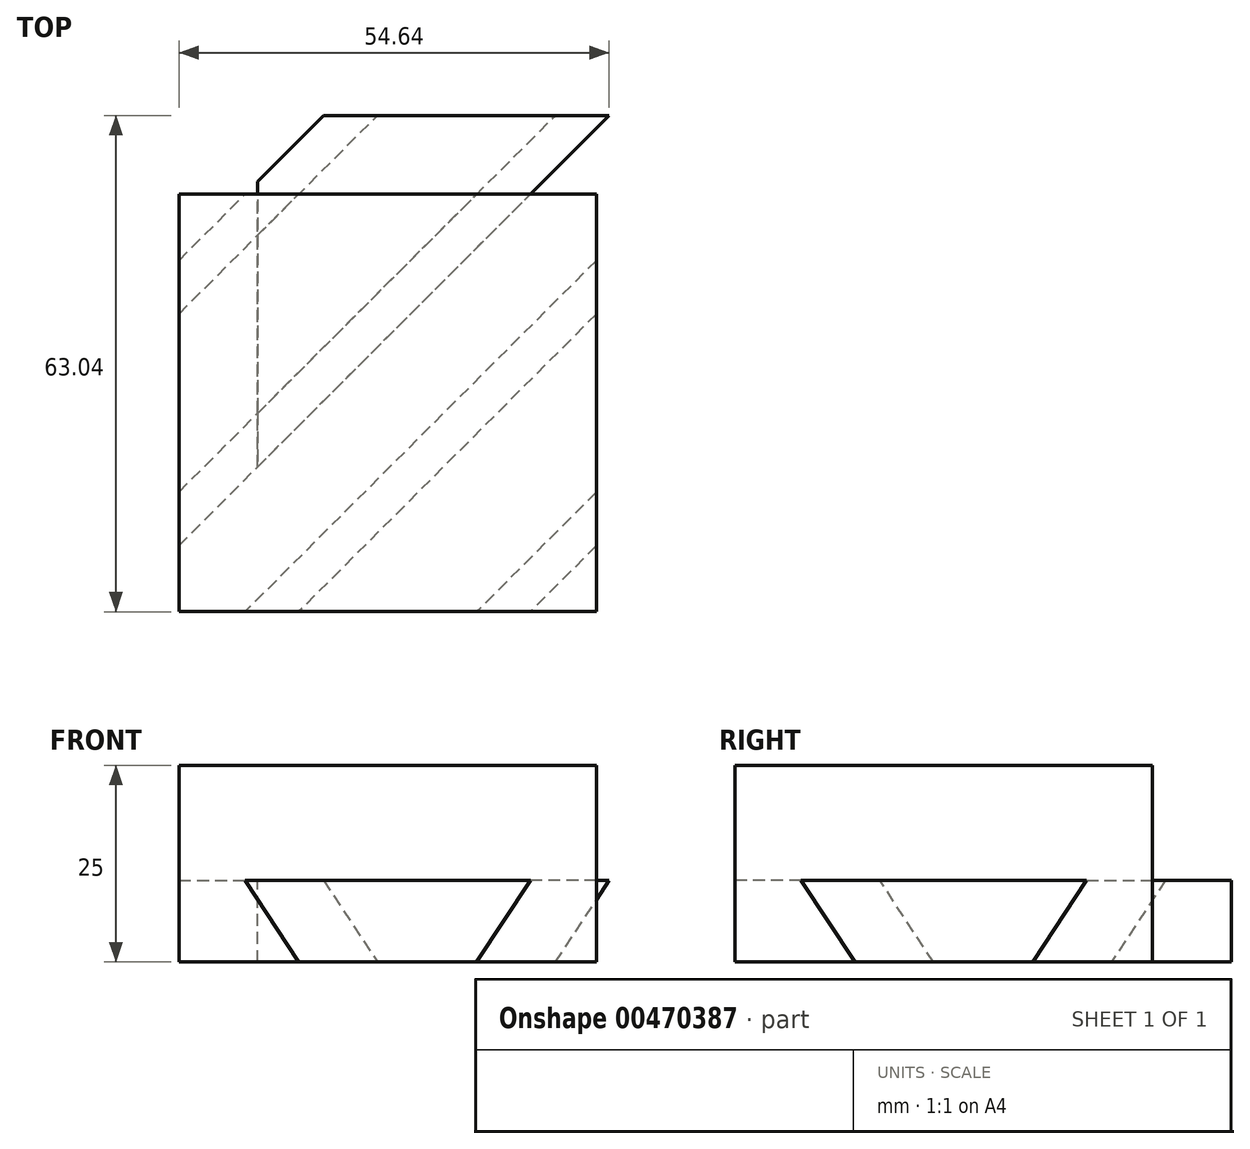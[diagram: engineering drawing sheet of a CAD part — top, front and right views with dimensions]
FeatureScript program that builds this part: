
annotation { "Feature Type Name" : "Feature", "Feature Type Description" : "" }
export const myFeature = defineFeature(function(context is Context, id is Id, definition is map)
    precondition{}
    {
        {
            var Q0;
            Q0=qCreatedBy(makeId("Top.planeOp"),FACE);
            var sketch = newSketch(context, id + "F0", { "sketchPlane" : qUnion([Q0])});
            skLineSegment(sketch, "E0.bottom", {"start": v(26.52, -26.52) * mm, "end": v(-26.52, -26.52) * mm});
            skLineSegment(sketch, "E0.top", {"start": v(26.52, 26.52) * mm, "end": v(-26.52, 26.52) * mm});
            skLineSegment(sketch, "E0.left", {"start": v(26.52, -26.52) * mm, "end": v(26.52, 26.52) * mm});
            skLineSegment(sketch, "E0.right", {"start": v(-26.52, -26.52) * mm, "end": v(-26.52, 26.52) * mm});
            skPoint(sketch, "E0.middle", {"position": v(0, 0) * mm});
            skSolve(sketch);
        }
        {
            var Q0;
            Q0=makeQuery(id+"F0.imprint","IMPRINT",FACE,{"disambiguationData":[TD([[makeQuery(id+"F0.imprint","IMPRINT",EDGE,{"derivedFrom":sQuery(id+"F0.wireOp",EDGE,"E0.bottom")}),-1.0]])]});
            extrude(context, id + "F1", {"entities" : qUnion([Q0]), "depth" : 25 * mm, "offsetDistance" : 25 * mm});
        }
        {
            var Q0;
            Q0=makeQuery(id+"F1.opExtrude","SWEPT_FACE",FACE,{"disambiguationData":[OSD([sQuery(id+"F0.wireOp",EDGE,"E0.bottom")])]});
            var sketch = newSketch(context, id + "F2", { "sketchPlane" : qUnion([Q0])});
            skLineSegment(sketch, "E1", {"start": v(-11.31, 25) * mm, "end": v(-18.12, 35.36) * mm});
            skLineSegment(sketch, "E2", {"start": v(-18.12, 35.36) * mm, "end": v(18.12, 35.36) * mm});
            skLineSegment(sketch, "E3", {"start": v(18.12, 35.36) * mm, "end": v(11.31, 25) * mm});
            skLineSegment(sketch, "E4", {"start": v(11.31, 25) * mm, "end": v(-11.31, 25) * mm});
            skPoint(sketch, "E5", {"position": v(0, 25) * mm});
            skLineSegment(sketch, "E6", {"start": v(0, 0) * mm, "end": v(0, 25) * mm, "construction": true});
            skSolve(sketch);
        }
        {
            var Q0;
            Q0=sQuery(id+"F2.wireOp",EDGE,"E6");
            cPlane(context, id + "F3", {"entities" : qUnion([Q0]), "cplaneType" : CPlaneType.LINE_ANGLE, "offset" : 25 * mm, "angle" : 45 * degree, "width" : 150 * mm, "height" : 150 * mm});
        }
        {
            var Q0;
            Q0=qCreatedBy(id+"F3.planeOp",FACE);
            var sketch = newSketch(context, id + "F4", { "sketchPlane" : qUnion([Q0])});
            skLineSegment(sketch, "E7.0.0", {"start": v(-5.94, 35.36) * mm, "end": v(-10.75, 25) * mm});
            skLineSegment(sketch, "E7.0.1", {"start": v(-10.75, 25) * mm, "end": v(-26.75, 25) * mm});
            skLineSegment(sketch, "E7.0.2", {"start": v(-26.75, 25) * mm, "end": v(-31.56, 35.36) * mm});
            skLineSegment(sketch, "E7.0.3", {"start": v(-31.56, 35.36) * mm, "end": v(-5.94, 35.36) * mm});
            skSolve(sketch);
        }
        {
            var Q0;
            Q0=makeQuery(id+"F1.opExtrude","CAP_FACE",FACE,{"disambiguationData":[OSD([sQuery(id+"F0.wireOp",EDGE,"E0.bottom"),sQuery(id+"F0.wireOp",EDGE,"E0.top"),sQuery(id+"F0.wireOp",EDGE,"E0.left"),sQuery(id+"F0.wireOp",EDGE,"E0.right")])],"isStart":false});
            extrude(context, id + "F5", {"entities" : qUnion([Q0]), "depth" : 41.2 * mm, "offsetDistance" : 25 * mm});
        }
        {
            var Q0;
            Q0=makeQuery(id+"F4.imprint","IMPRINT",FACE,{"disambiguationData":[TD([[makeQuery(id+"F4.imprint","IMPRINT",EDGE,{"derivedFrom":sQuery(id+"F4.wireOp",EDGE,"E7.0.0")}),-1.0]])]});
            extrude(context, id + "F6", {"entities" : qUnion([Q0]), "endBound" : BoundingType.SYMMETRIC, "depth" : 119 * mm, "offsetDistance" : 25 * mm});
        }
        {
            var Q0;
            Q0=makeQuery(id+"F1.opExtrude","CAP_FACE",FACE,{"disambiguationData":[OSD([sQuery(id+"F0.wireOp",EDGE,"E0.bottom"),sQuery(id+"F0.wireOp",EDGE,"E0.top"),sQuery(id+"F0.wireOp",EDGE,"E0.left"),sQuery(id+"F0.wireOp",EDGE,"E0.right")])],"isStart":false});
            extrude(context, id + "F7", {"entities" : qUnion([Q0]), "operationType" : NewBodyOperationType.INTERSECT, "depth" : 25 * mm, "offsetDistance" : 25 * mm});
        }
        {
            var Q0;
            Q0=qCreatedBy(makeId("Front.planeOp"),FACE);
            var sketch = newSketch(context, id + "F8", { "sketchPlane" : qUnion([Q0])});
            skLineSegment(sketch, "E8", {"start": v(0, 0) * mm, "end": v(0, 56.28) * mm, "construction": true});
            skSolve(sketch);
        }
        {
            var Q0;
            Q0=makeQuery(id+"F6.opExtrude","SWEPT_BODY",BODY,{"disambiguationData":[OSD([sQuery(id+"F4.wireOp",EDGE,"E7.0.0"),sQuery(id+"F4.wireOp",EDGE,"E7.0.1"),sQuery(id+"F4.wireOp",EDGE,"E7.0.2"),sQuery(id+"F4.wireOp",EDGE,"E7.0.3")])]});
            var Q1;
            Q1=sQuery(id+"F8.wireOp",EDGE,"E8");
            transform(context, id + "F9", {"entities" : qUnion([Q0]), "transformType" : TransformType.ROTATION, "transformAxis" : qUnion([Q1]), "angle" : 180 * degree, "makeCopy" : true});
        }
        {
            var Q0;
            Q0=makeQuery(id+"F9.opPattern","COPY",BODY,{"derivedFrom":makeQuery(id+"F6.opExtrude","SWEPT_BODY",BODY,{"disambiguationData":[OSD([sQuery(id+"F4.wireOp",EDGE,"E7.0.0"),sQuery(id+"F4.wireOp",EDGE,"E7.0.1"),sQuery(id+"F4.wireOp",EDGE,"E7.0.2"),sQuery(id+"F4.wireOp",EDGE,"E7.0.3")])]}),"instanceName":"1"});
            transform(context, id + "F10", {"entities" : qUnion([Q0]), "transformType" : TransformType.COPY});
        }
        {
            var Q0;
            Q0=makeQuery(id+"F10.opPattern","COPY",BODY,{"derivedFrom":makeQuery(id+"F9.opPattern","COPY",BODY,{"derivedFrom":makeQuery(id+"F6.opExtrude","SWEPT_BODY",BODY,{"disambiguationData":[OSD([sQuery(id+"F4.wireOp",EDGE,"E7.0.0"),sQuery(id+"F4.wireOp",EDGE,"E7.0.1"),sQuery(id+"F4.wireOp",EDGE,"E7.0.2"),sQuery(id+"F4.wireOp",EDGE,"E7.0.3")])]}),"instanceName":"1"}),"instanceName":"1"});
            var Q1;
            Q1=makeQuery(id+"F5.opExtrude","SWEPT_BODY",BODY,{"disambiguationData":[OSD([sQuery(id+"F0.wireOp",EDGE,"E0.bottom"),sQuery(id+"F0.wireOp",EDGE,"E0.top"),sQuery(id+"F0.wireOp",EDGE,"E0.left"),sQuery(id+"F0.wireOp",EDGE,"E0.right")])]});
            booleanBodies(context, id + "F11", {"operationType" : BooleanOperationType.SUBTRACTION, "tools" : qUnion([Q0]), "targets" : qUnion([Q1])});
        }
        {
            var Q0;
            Q0=makeQuery(id+"F9.opPattern","COPY",BODY,{"derivedFrom":makeQuery(id+"F6.opExtrude","SWEPT_BODY",BODY,{"disambiguationData":[OSD([sQuery(id+"F4.wireOp",EDGE,"E7.0.0"),sQuery(id+"F4.wireOp",EDGE,"E7.0.1"),sQuery(id+"F4.wireOp",EDGE,"E7.0.2"),sQuery(id+"F4.wireOp",EDGE,"E7.0.3")])]}),"instanceName":"1"});
            transform(context, id + "F12", {"entities" : qUnion([Q0]), "transformType" : TransformType.TRANSLATION_3D, "dx" : 10 * mm, "dy" : 10 * mm, "dz" : 0 * mm, "makeCopy" : false});
        }
    });
